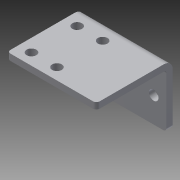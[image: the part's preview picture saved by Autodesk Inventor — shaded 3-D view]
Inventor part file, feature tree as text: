
AUTODESK INVENTOR PART (.ipt)
format: ipt  version: 2014 (Build 180170000, 170)  size: 197,120 bytes
history: native  units: in
note: dims shown in document units (in); Inventor stores cm internally (conversion verified against a paired STEP export)
features: sheet_metal_op x4, other x4, sketch x3, fillet x1, extrude x1
ambient origin geometry x8: Origin, YZ Plane, XZ Plane, XY Plane, X Axis, Y Axis, Z Axis, Center Point
bodies: Solid1 (feature_tree)
feature tree (13):
  sheet_metal_op  "Face1"
  sheet_metal_op  "Flange1"
  fillet  "Fillet1"  Radius=1.75in
  extrude  "Extrusion1"  Depth=0.19in
  sketch  "Sketch1"  dims[d1=1.0in d2=0.19in]
  other  "Plate1"
  sketch  "Sketch2"  dims[d4=0.7874in d6=1.0in d7=0.3937in d9=1.0in]
  other  "Plate2"
  sheet_metal_op  "Bend1"
  sheet_metal_op  "Corner1"
  sketch  "Sketch3"  dims[d11=0.125in d12=0.125in d13=0.0625in d14=0.25in d15=0.125in d16=1.5in d17=90.0deg d18=0.05in d19=0.5in d20=0.125in d21=0.125in d22=0.0625in d23=1.35in d24=0.75in d27=0.19in d28=0.125in d29=0.2265in d30=1.0in d31=0.0in d32=0.25in d33=0.875in d3=0.0in d5=0.0625in d8=0.0625in]
  other  "Definition1"
  other  "Cut1"
